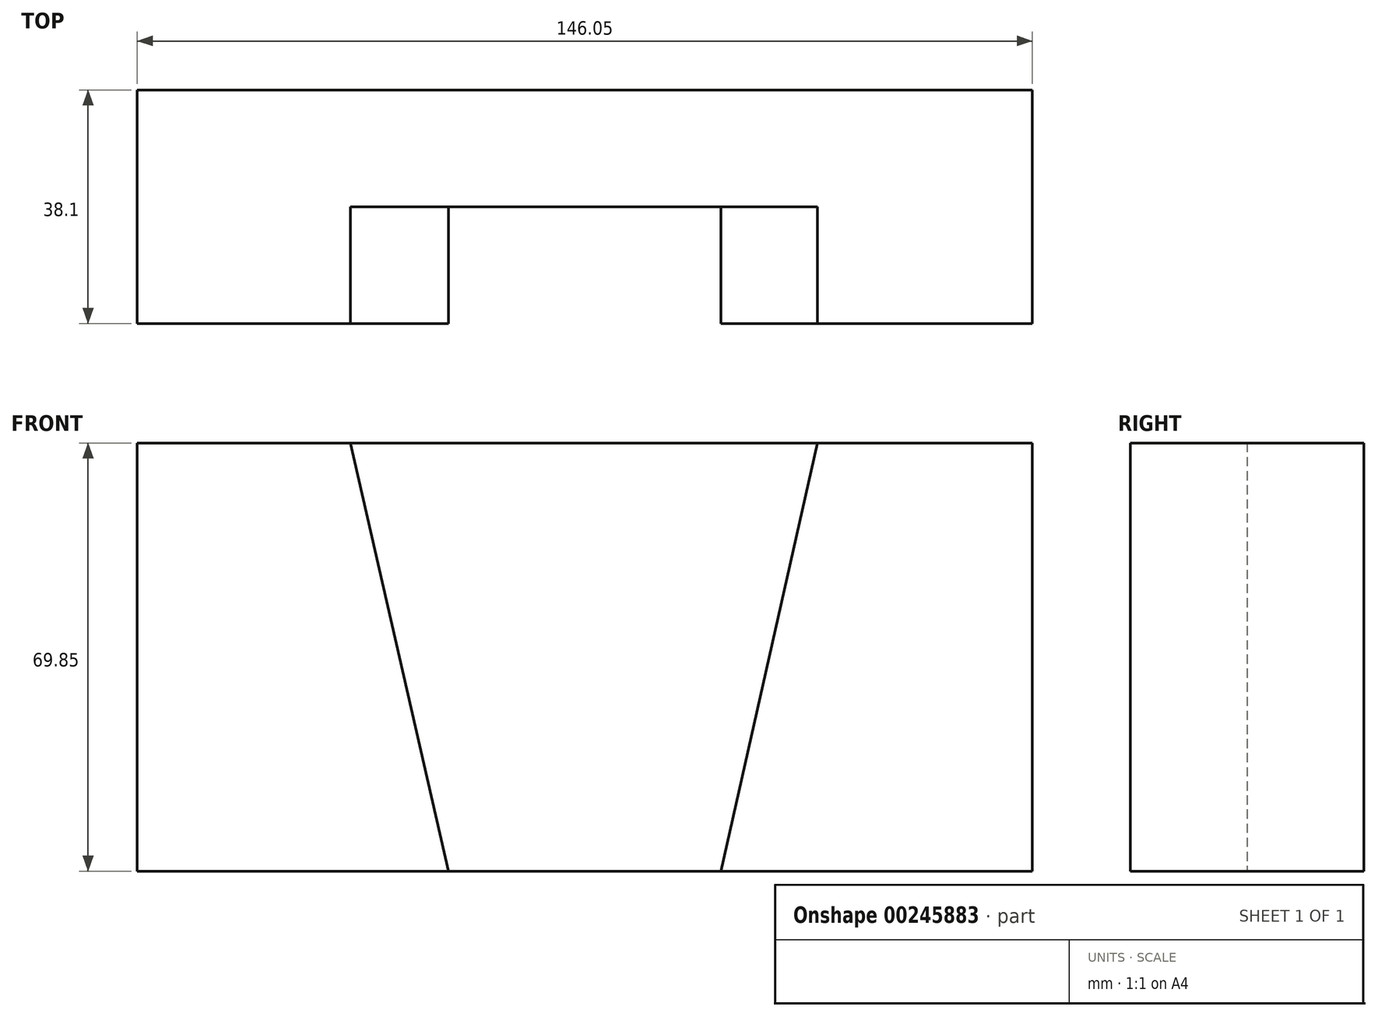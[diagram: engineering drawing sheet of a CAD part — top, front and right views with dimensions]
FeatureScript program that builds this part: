
annotation { "Feature Type Name" : "Feature", "Feature Type Description" : "" }
export const myFeature = defineFeature(function(context is Context, id is Id, definition is map)
    precondition{}
    {
        {
            var Q0;
            Q0=qCreatedBy(makeId("Front.planeOp"),FACE);
            var sketch = newSketch(context, id + "F0", { "sketchPlane" : qUnion([Q0])});
            skLineSegment(sketch, "E0", {"start": v(-68.13, -18.91) * mm, "end": v(77.92, -18.91) * mm});
            skLineSegment(sketch, "E1", {"start": v(-68.13, -18.91) * mm, "end": v(-68.13, 50.94) * mm});
            skLineSegment(sketch, "E2", {"start": v(-68.13, 50.94) * mm, "end": v(77.92, 50.94) * mm});
            skLineSegment(sketch, "E3", {"start": v(77.92, 50.94) * mm, "end": v(77.92, -18.91) * mm});
            skSolve(sketch);
        }
        {
            var Q0;
            Q0=makeQuery(id+"F0.imprint","IMPRINT",FACE,{"disambiguationData":[TD([[makeQuery(id+"F0.imprint","IMPRINT",EDGE,{"derivedFrom":sQuery(id+"F0.wireOp",EDGE,"E0")}),1.0]])]});
            extrude(context, id + "F1", {"entities" : qUnion([Q0]), "depth" : 38.1 * mm});
        }
        {
            var Q0;
            Q0=makeQuery(id+"F1.opExtrude","CAP_FACE",FACE,{"disambiguationData":[OSD([sQuery(id+"F0.wireOp",EDGE,"E0"),sQuery(id+"F0.wireOp",EDGE,"E1"),sQuery(id+"F0.wireOp",EDGE,"E2"),sQuery(id+"F0.wireOp",EDGE,"E3")])],"isStart":false});
            var sketch = newSketch(context, id + "F2", { "sketchPlane" : qUnion([Q0])});
            skLineSegment(sketch, "E4", {"start": v(77.92, -18.91) * mm, "end": v(27.12, -18.91) * mm});
            skLineSegment(sketch, "E5", {"start": v(27.12, -18.91) * mm, "end": v(-17.33, -18.91) * mm});
            skLineSegment(sketch, "E6", {"start": v(77.92, 50.94) * mm, "end": v(42.87, 50.94) * mm});
            skLineSegment(sketch, "E7", {"start": v(42.87, 50.94) * mm, "end": v(-33.33, 50.94) * mm});
            skLineSegment(sketch, "E8", {"start": v(-33.33, 50.94) * mm, "end": v(-17.33, -18.91) * mm});
            skLineSegment(sketch, "E9", {"start": v(42.87, 50.94) * mm, "end": v(27.12, -18.91) * mm});
            skSolve(sketch);
        }
        {
            var Q0;
            Q0 = qSketchRegion(id + "F2", true);
            extrude(context, id + "F3", {"entities" : qUnion([Q0]), "operationType" : NewBodyOperationType.REMOVE, "oppositeDirection" : true, "depth" : 19.05 * mm});
        }
    });
